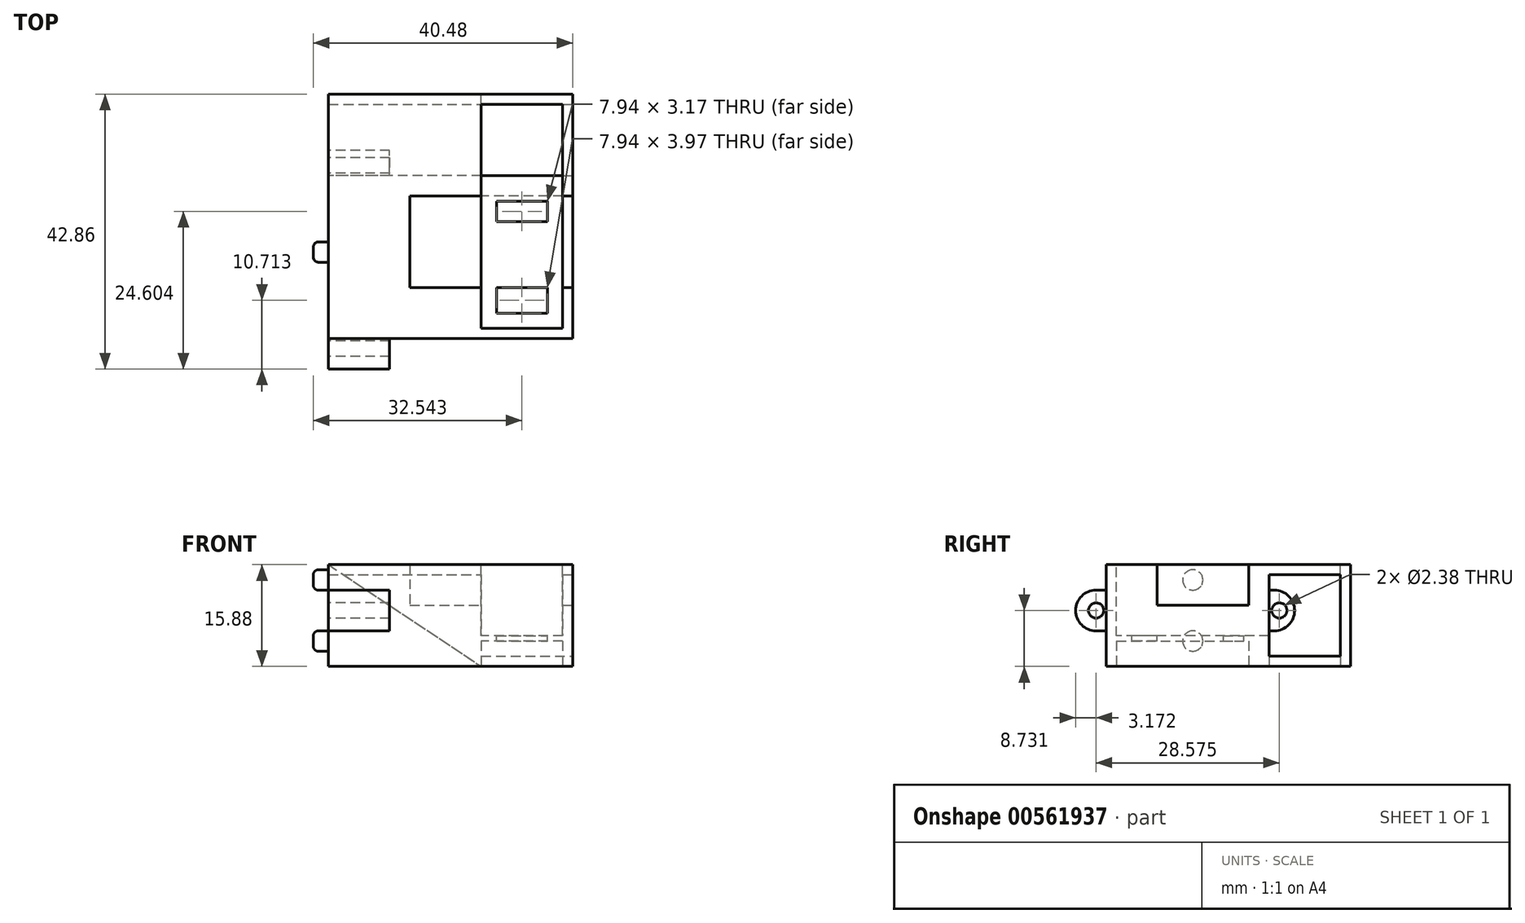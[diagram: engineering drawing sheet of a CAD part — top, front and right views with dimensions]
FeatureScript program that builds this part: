
annotation { "Feature Type Name" : "Feature", "Feature Type Description" : "" }
export const myFeature = defineFeature(function(context is Context, id is Id, definition is map)
    precondition{}
    {
        {
            var Q0;
            Q0=qCreatedBy(makeId("Top.planeOp"),FACE);
            var sketch = newSketch(context, id + "F0", { "sketchPlane" : qUnion([Q0])});
            skLineSegment(sketch, "E0.bottom", {"start": v(19.05, 19.05) * mm, "end": v(-19.05, 19.05) * mm});
            skLineSegment(sketch, "E0.top", {"start": v(19.05, -19.05) * mm, "end": v(-19.05, -19.05) * mm});
            skLineSegment(sketch, "E0.left", {"start": v(19.05, 19.05) * mm, "end": v(19.05, -19.05) * mm});
            skLineSegment(sketch, "E0.right", {"start": v(-19.05, 19.05) * mm, "end": v(-19.05, -19.05) * mm});
            skPoint(sketch, "E0.middle", {"position": v(0, 0) * mm});
            skSolve(sketch);
        }
        {
            var Q0;
            Q0 = qSketchRegion(id + "F0", true);
            extrude(context, id + "F1", {"entities" : qUnion([Q0]), "depth" : 15.88 * mm, "offsetDistance" : 25.4 * mm});
        }
        {
            var Q0;
            Q0=makeQuery(id+"F1.opExtrude","CAP_FACE",FACE,{"disambiguationData":[OSD([sQuery(id+"F0.wireOp",EDGE,"E0.bottom"),sQuery(id+"F0.wireOp",EDGE,"E0.top"),sQuery(id+"F0.wireOp",EDGE,"E0.left"),sQuery(id+"F0.wireOp",EDGE,"E0.right")])],"isStart":false});
            var sketch = newSketch(context, id + "F2", { "sketchPlane" : qUnion([Q0])});
            skLineSegment(sketch, "E1.bottom", {"start": v(17.46, 17.46) * mm, "end": v(4.76, 17.46) * mm});
            skLineSegment(sketch, "E1.top", {"start": v(17.46, -17.46) * mm, "end": v(4.76, -17.46) * mm});
            skLineSegment(sketch, "E1.left", {"start": v(17.46, 17.46) * mm, "end": v(17.46, -17.46) * mm});
            skLineSegment(sketch, "E1.right", {"start": v(4.76, 17.46) * mm, "end": v(4.76, -17.46) * mm});
            skPoint(sketch, "E1.middle", {"position": v(11.11, 0) * mm});
            skSolve(sketch);
        }
        {
            var Q0;
            Q0 = qSketchRegion(id + "F2", true);
            extrude(context, id + "F3", {"entities" : qUnion([Q0]), "operationType" : NewBodyOperationType.REMOVE, "oppositeDirection" : true, "depth" : 11.1 * mm, "offsetDistance" : 25.4 * mm});
        }
        {
            var Q0;
            Q0=makeQuery(id+"F1.opExtrude","SWEPT_FACE",FACE,{"disambiguationData":[OSD([sQuery(id+"F0.wireOp",EDGE,"E0.left")])]});
            var sketch = newSketch(context, id + "F4", { "sketchPlane" : qUnion([Q0])});
            skLineSegment(sketch, "E2.bottom", {"start": v(6.35, 1.59) * mm, "end": v(17.46, 1.59) * mm});
            skLineSegment(sketch, "E2.top", {"start": v(6.35, 14.29) * mm, "end": v(17.46, 14.29) * mm});
            skLineSegment(sketch, "E2.left", {"start": v(6.35, 1.59) * mm, "end": v(6.35, 14.29) * mm});
            skLineSegment(sketch, "E2.right", {"start": v(17.46, 1.59) * mm, "end": v(17.46, 14.29) * mm});
            skPoint(sketch, "E2.middle", {"position": v(11.9, 7.94) * mm});
            skSolve(sketch);
        }
        {
            var Q0;
            Q0 = qSketchRegion(id + "F4", true);
            extrude(context, id + "F5", {"entities" : qUnion([Q0]), "operationType" : NewBodyOperationType.REMOVE, "endBound" : BoundingType.THROUGH_ALL, "oppositeDirection" : true, "depth" : 12.7 * mm, "offsetDistance" : 25.4 * mm});
        }
        {
            var Q0;
            Q0=makeQuery(id+"F1.opExtrude","CAP_FACE",FACE,{"disambiguationData":[OSD([sQuery(id+"F0.wireOp",EDGE,"E0.bottom"),sQuery(id+"F0.wireOp",EDGE,"E0.top"),sQuery(id+"F0.wireOp",EDGE,"E0.left"),sQuery(id+"F0.wireOp",EDGE,"E0.right")])],"isStart":true});
            var sketch = newSketch(context, id + "F6", { "sketchPlane" : qUnion([Q0])});
            skLineSegment(sketch, "E3.bottom", {"start": v(4.76, -6.35) * mm, "end": v(-19.05, -6.35) * mm});
            skLineSegment(sketch, "E3.top", {"start": v(4.76, -17.46) * mm, "end": v(-19.05, -17.46) * mm});
            skLineSegment(sketch, "E3.left", {"start": v(4.76, -6.35) * mm, "end": v(4.76, -17.46) * mm});
            skLineSegment(sketch, "E3.right", {"start": v(-19.05, -6.35) * mm, "end": v(-19.05, -17.46) * mm});
            skPoint(sketch, "E3.middle", {"position": v(-7.14, -11.9) * mm});
            skSolve(sketch);
        }
        {
            var Q0;
            Q0 = qSketchRegion(id + "F6", true);
            extrude(context, id + "F7", {"entities" : qUnion([Q0]), "operationType" : NewBodyOperationType.REMOVE, "endBound" : BoundingType.UP_TO_NEXT, "oppositeDirection" : true, "depth" : 1.59 * mm, "offsetDistance" : 25.4 * mm});
        }
        {
            var Q0;
            Q0=makeQuery(id+"F3.boolean.opBoolean","COPY",FACE,{"derivedFrom":makeQuery(id+"F3.opExtrude","CAP_FACE",FACE,{"disambiguationData":[OSD([sQuery(id+"F2.wireOp",EDGE,"E1.bottom"),sQuery(id+"F2.wireOp",EDGE,"E1.top"),sQuery(id+"F2.wireOp",EDGE,"E1.left"),sQuery(id+"F2.wireOp",EDGE,"E1.right")])],"isStart":false})});
            var sketch = newSketch(context, id + "F8", { "sketchPlane" : qUnion([Q0])});
            skLineSegment(sketch, "E4.bottom", {"start": v(15.08, -0.8) * mm, "end": v(7.14, -0.8) * mm});
            skLineSegment(sketch, "E4.top", {"start": v(15.08, 2.38) * mm, "end": v(7.14, 2.38) * mm});
            skLineSegment(sketch, "E4.left", {"start": v(15.08, -0.8) * mm, "end": v(15.08, 2.38) * mm});
            skLineSegment(sketch, "E4.right", {"start": v(7.14, -0.8) * mm, "end": v(7.14, 2.38) * mm});
            skPoint(sketch, "E4.middle", {"position": v(11.11, 0.8) * mm});
            skLineSegment(sketch, "E5.bottom", {"start": v(7.14, -11.11) * mm, "end": v(15.08, -11.11) * mm});
            skLineSegment(sketch, "E5.top", {"start": v(7.14, -15.08) * mm, "end": v(15.08, -15.08) * mm});
            skLineSegment(sketch, "E5.left", {"start": v(7.14, -11.11) * mm, "end": v(7.14, -15.08) * mm});
            skLineSegment(sketch, "E5.right", {"start": v(15.08, -11.11) * mm, "end": v(15.08, -15.08) * mm});
            skPoint(sketch, "E5.middle", {"position": v(11.11, -13.1) * mm});
            skSolve(sketch);
        }
        {
            var Q0;
            Q0 = qSketchRegion(id + "F8", true);
            extrude(context, id + "F9", {"entities" : qUnion([Q0]), "operationType" : NewBodyOperationType.REMOVE, "endBound" : BoundingType.UP_TO_NEXT, "oppositeDirection" : true, "depth" : 25.4 * mm, "offsetDistance" : 25.4 * mm});
        }
        {
            var Q0;
            Q0=makeQuery(id+"F1.opExtrude","SWEPT_FACE",FACE,{"disambiguationData":[OSD([sQuery(id+"F0.wireOp",EDGE,"E0.bottom")])]});
            var sketch = newSketch(context, id + "F10", { "sketchPlane" : qUnion([Q0])});
            skLineSegment(sketch, "E6", {"start": v(19.05, 15.88) * mm, "end": v(-4.76, 0) * mm});
            skLineSegment(sketch, "E7", {"start": v(-4.76, 0) * mm, "end": v(19.05, 0) * mm});
            skLineSegment(sketch, "E8", {"start": v(19.05, 0) * mm, "end": v(19.05, 15.88) * mm});
            skSolve(sketch);
        }
        {
            var Q0;
            Q0 = qSketchRegion(id + "F10", true);
            extrude(context, id + "F11", {"entities" : qUnion([Q0]), "operationType" : NewBodyOperationType.REMOVE, "oppositeDirection" : true, "depth" : 1.59 * mm, "offsetDistance" : 25.4 * mm});
        }
        {
            var Q0;
            Q0=makeQuery(id+"F1.opExtrude","SWEPT_FACE",FACE,{"disambiguationData":[OSD([sQuery(id+"F0.wireOp",EDGE,"E0.right")])]});
            var sketch = newSketch(context, id + "F12", { "sketchPlane" : qUnion([Q0])});
            skLineSegment(sketch, "E9", {"start": v(-6.35, 11.9) * mm, "end": v(-7.14, 11.9) * mm});
            skLineSegment(sketch, "E10", {"start": v(-6.35, 5.56) * mm, "end": v(-7.14, 5.56) * mm});
            skArc(sketch, "E11", {"start": v(-7.14, 11.9) * mm, "mid": v(-10.32, 8.73) * mm, "end": v(-7.14, 5.56) * mm});
            skCircle(sketch, "E12", {"center": v(-7.94, 8.73) * mm, "radius": 1.2 * mm});
            skPoint(sketch, "E13", {"position": v(-10.32, 8.73) * mm});
            skPoint(sketch, "E13.positionSnap0", {"position": v(-10.32, 8.73) * mm});
            skLineSegment(sketch, "E14", {"start": v(-7.14, 11.9) * mm, "end": v(-7.14, 5.56) * mm, "construction": true});
            skSolve(sketch);
        }
        {
            var Q0;
            {var subQ1=sQuery(id+"F12.wireOp",EDGE,"E9");Q0=makeQuery(id+"F12.imprint","IMPRINT",FACE,{"disambiguationData":[TD([[makeQuery(id+"F12.imprint","IMPRINT",EDGE,{"derivedFrom":subQ1}),1.0]])]});}
            extrude(context, id + "F13", {"entities" : qUnion([Q0]), "operationType" : NewBodyOperationType.ADD, "oppositeDirection" : true, "depth" : 9.52 * mm, "offsetDistance" : 25.4 * mm});
        }
        {
            var Q0;
            {var subQ0=sQuery(id+"F0.wireOp",EDGE,"E0.right");Q0=makeQuery(id+"F13.boolean.opBoolean","MERGE",FACE,{"derivedFrom":[makeQuery(id+"F1.opExtrude","SWEPT_FACE",FACE,{"disambiguationData":[OSD([subQ0])]}),makeQuery(id+"F13.opExtrude","CAP_FACE",FACE,{"disambiguationData":[OSD([subQ0,sQuery(id+"F4.wireOp",EDGE,"E2.bottom"),sQuery(id+"F4.wireOp",EDGE,"E2.left"),sQuery(id+"F12.wireOp",EDGE,"E9"),sQuery(id+"F12.wireOp",EDGE,"E10"),sQuery(id+"F12.wireOp",EDGE,"E11"),sQuery(id+"F12.wireOp",EDGE,"E12")])],"isStart":true})]});}
            var sketch = newSketch(context, id + "F14", { "sketchPlane" : qUnion([Q0])});
            skLineSegment(sketch, "E15", {"start": v(19.05, 11.9) * mm, "end": v(20.64, 11.9) * mm});
            skLineSegment(sketch, "E16", {"start": v(19.05, 5.56) * mm, "end": v(20.64, 5.56) * mm});
            skArc(sketch, "E17", {"start": v(20.64, 5.56) * mm, "mid": v(23.81, 8.73) * mm, "end": v(20.64, 11.9) * mm});
            skPoint(sketch, "E18", {"position": v(23.81, 8.73) * mm});
            skLineSegment(sketch, "E19", {"start": v(20.64, 11.9) * mm, "end": v(20.64, 5.56) * mm, "construction": true});
            skLineSegment(sketch, "E20", {"start": v(-6.35, 11.9) * mm, "end": v(19.05, 11.9) * mm, "construction": true});
            skLineSegment(sketch, "E21", {"start": v(-6.35, 5.56) * mm, "end": v(19.05, 5.56) * mm, "construction": true});
            skCircle(sketch, "E22", {"center": v(20.64, 8.73) * mm, "radius": 1.2 * mm});
            skLineSegment(sketch, "E23", {"start": v(-7.94, 8.73) * mm, "end": v(20.64, 8.73) * mm, "construction": true});
            skSolve(sketch);
        }
        {
            var Q0;
            {var subQ1=sQuery(id+"F14.wireOp",EDGE,"E15");Q0=makeQuery(id+"F14.imprint","IMPRINT",FACE,{"disambiguationData":[TD([[makeQuery(id+"F14.imprint","IMPRINT",EDGE,{"derivedFrom":subQ1}),-1.0]])]});}
            extrude(context, id + "F15", {"entities" : qUnion([Q0]), "operationType" : NewBodyOperationType.ADD, "oppositeDirection" : true, "depth" : 9.52 * mm, "offsetDistance" : 25.4 * mm});
        }
        {
            var Q0;
            Q0=makeQuery(id+"F1.opExtrude","CAP_FACE",FACE,{"disambiguationData":[OSD([sQuery(id+"F0.wireOp",EDGE,"E0.bottom"),sQuery(id+"F0.wireOp",EDGE,"E0.top"),sQuery(id+"F0.wireOp",EDGE,"E0.left"),sQuery(id+"F0.wireOp",EDGE,"E0.right")])],"isStart":true});
            var sketch = newSketch(context, id + "F16", { "sketchPlane" : qUnion([Q0])});
            skLineSegment(sketch, "E24.bottom", {"start": v(17.46, 17.46) * mm, "end": v(4.76, 17.46) * mm});
            skLineSegment(sketch, "E24.top", {"start": v(17.46, -3.17) * mm, "end": v(4.76, -3.17) * mm});
            skLineSegment(sketch, "E24.left", {"start": v(17.46, 17.46) * mm, "end": v(17.46, -3.17) * mm});
            skLineSegment(sketch, "E24.right", {"start": v(4.76, 17.46) * mm, "end": v(4.76, -3.17) * mm});
            skPoint(sketch, "E24.middle", {"position": v(11.11, 7.14) * mm});
            skSolve(sketch);
        }
        {
            var Q0;
            Q0 = qSketchRegion(id + "F16", true);
            extrude(context, id + "F17", {"entities" : qUnion([Q0]), "operationType" : NewBodyOperationType.REMOVE, "oppositeDirection" : true, "depth" : 3.97 * mm, "offsetDistance" : 25.4 * mm});
        }
        {
            var Q0;
            Q0=makeQuery(id+"F1.opExtrude","SWEPT_FACE",FACE,{"disambiguationData":[OSD([sQuery(id+"F0.wireOp",EDGE,"E0.left")])]});
            var sketch = newSketch(context, id + "F18", { "sketchPlane" : qUnion([Q0])});
            skLineSegment(sketch, "E25.bottom", {"start": v(3.17, 15.88) * mm, "end": v(-11.11, 15.88) * mm});
            skLineSegment(sketch, "E25.top", {"start": v(3.17, 9.53) * mm, "end": v(-11.11, 9.53) * mm});
            skLineSegment(sketch, "E25.left", {"start": v(3.17, 15.88) * mm, "end": v(3.17, 9.53) * mm});
            skLineSegment(sketch, "E25.right", {"start": v(-11.11, 15.88) * mm, "end": v(-11.11, 9.53) * mm});
            skPoint(sketch, "E25.middle", {"position": v(-3.97, 12.7) * mm});
            skSolve(sketch);
        }
        {
            var Q0;
            Q0 = qSketchRegion(id + "F18", true);
            extrude(context, id + "F19", {"entities" : qUnion([Q0]), "operationType" : NewBodyOperationType.REMOVE, "oppositeDirection" : true, "depth" : 25.4 * mm, "offsetDistance" : 25.4 * mm});
        }
        {
            var Q0;
            {var subQ0=sQuery(id+"F0.wireOp",EDGE,"E0.right");Q0=makeQuery(id+"F15.boolean.opBoolean","MERGE",FACE,{"derivedFrom":[makeQuery(id+"F13.boolean.opBoolean","MERGE",FACE,{"derivedFrom":[makeQuery(id+"F1.opExtrude","SWEPT_FACE",FACE,{"disambiguationData":[OSD([subQ0])]}),makeQuery(id+"F13.opExtrude","CAP_FACE",FACE,{"disambiguationData":[OSD([subQ0,sQuery(id+"F4.wireOp",EDGE,"E2.bottom"),sQuery(id+"F4.wireOp",EDGE,"E2.left"),sQuery(id+"F12.wireOp",EDGE,"E9"),sQuery(id+"F12.wireOp",EDGE,"E10"),sQuery(id+"F12.wireOp",EDGE,"E11"),sQuery(id+"F12.wireOp",EDGE,"E12")])],"isStart":true})]}),makeQuery(id+"F15.opExtrude","CAP_FACE",FACE,{"disambiguationData":[OSD([sQuery(id+"F0.wireOp",EDGE,"E0.top"),subQ0,sQuery(id+"F14.wireOp",EDGE,"E15"),sQuery(id+"F14.wireOp",EDGE,"E16"),sQuery(id+"F14.wireOp",EDGE,"E17"),sQuery(id+"F14.wireOp",EDGE,"E22")])],"isStart":true})]});}
            var sketch = newSketch(context, id + "F20", { "sketchPlane" : qUnion([Q0])});
            skCircle(sketch, "E26", {"center": v(5.56, 13.5) * mm, "radius": 1.59 * mm});
            skCircle(sketch, "E27", {"center": v(5.56, 3.97) * mm, "radius": 1.59 * mm});
            skSolve(sketch);
        }
        {
            var Q0;
            Q0 = qSketchRegion(id + "F20", true);
            extrude(context, id + "F21", {"entities" : qUnion([Q0]), "operationType" : NewBodyOperationType.ADD, "depth" : 2.38 * mm, "offsetDistance" : 25.4 * mm});
        }
        {
            var Q0;
            Q0=makeQuery(id+"F21.opExtrude","CAP_EDGE",EDGE,{"disambiguationData":[OSD([sQuery(id+"F20.wireOp",EDGE,"E26")])],"isStart":false});
            var Q1;
            Q1=makeQuery(id+"F21.opExtrude","CAP_FACE",FACE,{"disambiguationData":[OSD([sQuery(id+"F20.wireOp",EDGE,"E27")])],"isStart":false});
            fillet(context, id + "F22", {"entities" : qUnion([Q0, Q1]), "radius" : 0.8 * mm, "tangentPropagation" : true, "allowEdgeOverflow" : false});
        }
    });
